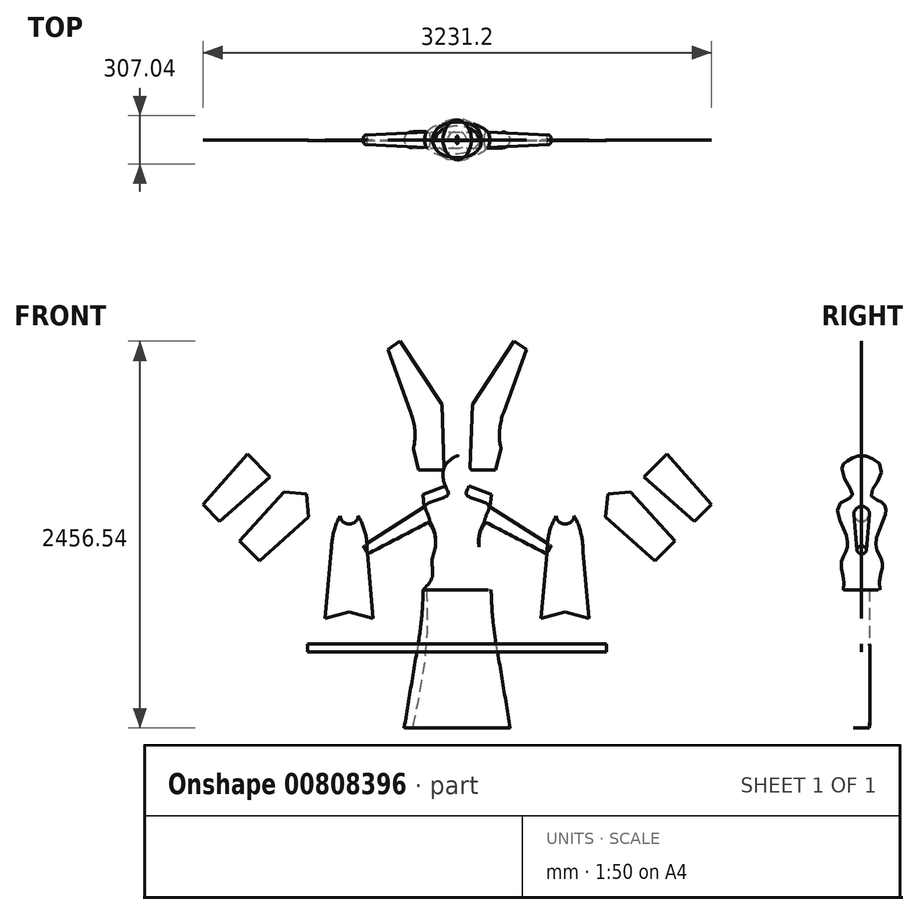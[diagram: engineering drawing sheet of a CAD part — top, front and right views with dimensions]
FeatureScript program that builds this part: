
annotation { "Feature Type Name" : "Feature", "Feature Type Description" : "" }
export const myFeature = defineFeature(function(context is Context, id is Id, definition is map)
    precondition{}
    {
        {
            var Q0;
            Q0=qCreatedBy(makeId("Front.planeOp"),FACE);
            var sketch = newSketch(context, id + "F0", { "sketchPlane" : qUnion([Q0])});
            skLineSegment(sketch, "E0", {"start": v(0, 0) * mm, "end": v(0, -1727.2) * mm, "construction": true});
            skPoint(sketch, "E1", {"position": v(0, -50.8) * mm});
            skPoint(sketch, "E2", {"position": v(0, -203.2) * mm});
            skPoint(sketch, "E3", {"position": v(0, -241.3) * mm});
            skPoint(sketch, "E4", {"position": v(0, -304.8) * mm});
            skPoint(sketch, "E5", {"position": v(0, -431.8) * mm});
            skPoint(sketch, "E6", {"position": v(0, -609.6) * mm});
            skPoint(sketch, "E7", {"position": v(0, -660.4) * mm});
            skPoint(sketch, "E8", {"position": v(0, -787.4) * mm});
            skPoint(sketch, "E9", {"position": v(0, -850.9) * mm});
            skPoint(sketch, "E10", {"position": v(0, -1193.8) * mm});
            skSolve(sketch);
        }
        {
            var Q0;
            Q0=qCreatedBy(makeId("Top.planeOp"),FACE);
            var Q1;
            Q1=sQuery(id+"F0.wireOp",VERTEX,"E1");
            cPlane(context, id + "F1", {"entities" : qUnion([Q0, Q1]), "cplaneType" : CPlaneType.PLANE_POINT, "offset" : 25.4 * mm, "width" : 152.4 * mm, "height" : 152.4 * mm});
        }
        {
            var Q0;
            Q0=sQuery(id+"F0.wireOp",VERTEX,"E2");
            var Q1;
            Q1=qCreatedBy(makeId("Top.planeOp"),FACE);
            cPlane(context, id + "F2", {"entities" : qUnion([Q0, Q1]), "cplaneType" : CPlaneType.PLANE_POINT, "offset" : 25.4 * mm, "width" : 152.4 * mm, "height" : 152.4 * mm});
        }
        {
            var Q0;
            Q0=qCreatedBy(makeId("Top.planeOp"),FACE);
            var Q1;
            Q1=sQuery(id+"F0.wireOp",VERTEX,"E3");
            cPlane(context, id + "F3", {"entities" : qUnion([Q0, Q1]), "cplaneType" : CPlaneType.PLANE_POINT, "offset" : 25.4 * mm, "width" : 152.4 * mm, "height" : 152.4 * mm});
        }
        {
            var Q0;
            Q0=sQuery(id+"F0.wireOp",VERTEX,"E4");
            var Q1;
            Q1=qCreatedBy(makeId("Top.planeOp"),FACE);
            cPlane(context, id + "F4", {"entities" : qUnion([Q0, Q1]), "cplaneType" : CPlaneType.PLANE_POINT, "offset" : 25.4 * mm, "width" : 152.4 * mm, "height" : 152.4 * mm});
        }
        {
            var Q0;
            Q0=sQuery(id+"F0.wireOp",VERTEX,"E5");
            var Q1;
            Q1=qCreatedBy(makeId("Top.planeOp"),FACE);
            cPlane(context, id + "F5", {"entities" : qUnion([Q0, Q1]), "cplaneType" : CPlaneType.PLANE_POINT, "offset" : 25.4 * mm, "width" : 152.4 * mm, "height" : 152.4 * mm});
        }
        {
            var Q0;
            Q0=sQuery(id+"F0.wireOp",VERTEX,"E6");
            var Q1;
            Q1=qCreatedBy(makeId("Top.planeOp"),FACE);
            cPlane(context, id + "F6", {"entities" : qUnion([Q0, Q1]), "cplaneType" : CPlaneType.PLANE_POINT, "offset" : 25.4 * mm, "width" : 152.4 * mm, "height" : 152.4 * mm});
        }
        {
            var Q0;
            Q0=sQuery(id+"F0.wireOp",VERTEX,"E7");
            var Q1;
            Q1=qCreatedBy(makeId("Top.planeOp"),FACE);
            cPlane(context, id + "F7", {"entities" : qUnion([Q0, Q1]), "cplaneType" : CPlaneType.PLANE_POINT, "offset" : 25.4 * mm, "width" : 152.4 * mm, "height" : 152.4 * mm});
        }
        {
            var Q0;
            Q0=qCreatedBy(makeId("Top.planeOp"),FACE);
            var Q1;
            Q1=sQuery(id+"F0.wireOp",VERTEX,"E8");
            cPlane(context, id + "F8", {"entities" : qUnion([Q0, Q1]), "cplaneType" : CPlaneType.PLANE_POINT, "offset" : 25.4 * mm, "width" : 152.4 * mm, "height" : 152.4 * mm});
        }
        {
            var Q0;
            Q0=sQuery(id+"F0.wireOp",VERTEX,"E9");
            var Q1;
            Q1=qCreatedBy(makeId("Top.planeOp"),FACE);
            cPlane(context, id + "F9", {"entities" : qUnion([Q0, Q1]), "cplaneType" : CPlaneType.PLANE_POINT, "offset" : 25.4 * mm, "width" : 152.4 * mm, "height" : 152.4 * mm});
        }
        {
            var Q0;
            Q0=sQuery(id+"F0.wireOp",VERTEX,"E10");
            var Q1;
            Q1=qCreatedBy(makeId("Top.planeOp"),FACE);
            cPlane(context, id + "F10", {"entities" : qUnion([Q0, Q1]), "cplaneType" : CPlaneType.PLANE_POINT, "offset" : 25.4 * mm, "width" : 152.4 * mm, "height" : 152.4 * mm});
        }
        {
            var Q0;
            Q0=sQuery(id+"F0.wireOp",VERTEX,"E0.end");
            var Q1;
            Q1=qCreatedBy(makeId("Top.planeOp"),FACE);
            cPlane(context, id + "F11", {"entities" : qUnion([Q0, Q1]), "cplaneType" : CPlaneType.PLANE_POINT, "offset" : 25.4 * mm, "width" : 152.4 * mm, "height" : 152.4 * mm});
        }
        {
            var Q0;
            Q0=qCreatedBy(id+"F11.planeOp",FACE);
            var sketch = newSketch(context, id + "F12", { "sketchPlane" : qUnion([Q0])});
            skLineSegment(sketch, "E11.bottom", {"start": v(-285.75, 50.8) * mm, "end": v(285.75, 50.8) * mm});
            skLineSegment(sketch, "E11.top", {"start": v(-285.75, -50.8) * mm, "end": v(285.75, -50.8) * mm});
            skLineSegment(sketch, "E11.left", {"start": v(-285.75, 50.8) * mm, "end": v(-285.75, -50.8) * mm, "construction": true});
            skLineSegment(sketch, "E11.right", {"start": v(285.75, 50.8) * mm, "end": v(285.75, -50.8) * mm, "construction": true});
            skPoint(sketch, "E11.middle", {"position": v(0, 0) * mm});
            skArc(sketch, "E12", {"start": v(-285.75, 50.8) * mm, "mid": v(-336.55, 0) * mm, "end": v(-285.75, -50.8) * mm});
            skArc(sketch, "E13", {"start": v(285.75, -50.8) * mm, "mid": v(336.55, 0) * mm, "end": v(285.75, 50.8) * mm});
            skPoint(sketch, "E14", {"position": v(-336.55, 0) * mm});
            skPoint(sketch, "E15", {"position": v(336.55, 0) * mm});
            skSolve(sketch);
        }
        {
            var Q0;
            Q0=qCreatedBy(id+"F10.planeOp",FACE);
            var sketch = newSketch(context, id + "F13", { "sketchPlane" : qUnion([Q0])});
            skLineSegment(sketch, "E16.bottom", {"start": v(-196.85, 50.8) * mm, "end": v(196.85, 50.8) * mm});
            skLineSegment(sketch, "E16.top", {"start": v(-196.85, -50.8) * mm, "end": v(196.85, -50.8) * mm});
            skLineSegment(sketch, "E16.left", {"start": v(-196.85, 50.8) * mm, "end": v(-196.85, -50.8) * mm, "construction": true});
            skLineSegment(sketch, "E16.right", {"start": v(196.85, 50.8) * mm, "end": v(196.85, -50.8) * mm, "construction": true});
            skPoint(sketch, "E16.middle", {"position": v(0, 0) * mm});
            skArc(sketch, "E17", {"start": v(-196.85, 50.8) * mm, "mid": v(-247.65, 0) * mm, "end": v(-196.85, -50.8) * mm});
            skArc(sketch, "E18", {"start": v(196.85, -50.8) * mm, "mid": v(247.65, 0) * mm, "end": v(196.85, 50.8) * mm});
            skPoint(sketch, "E19", {"position": v(247.65, 0) * mm});
            skPoint(sketch, "E20", {"position": v(-247.65, 0) * mm});
            skSolve(sketch);
        }
        {
            var Q0;
            Q0=qCreatedBy(id+"F9.planeOp",FACE);
            var sketch = newSketch(context, id + "F14", { "sketchPlane" : qUnion([Q0])});
            skEllipse(sketch, "E21", {"center": v(0, 0) * mm, "majorRadius": 215.9 * mm, "minorRadius": 114.3 * mm, "majorAxis": v(-1, 0)});
            skSolve(sketch);
        }
        {
            var Q0;
            Q0=qCreatedBy(id+"F8.planeOp",FACE);
            var sketch = newSketch(context, id + "F15", { "sketchPlane" : qUnion([Q0])});
            skEllipse(sketch, "E22", {"center": v(0, 0) * mm, "majorRadius": 165.1 * mm, "minorRadius": 114.3 * mm, "majorAxis": v(-1, 0)});
            skSolve(sketch);
        }
        {
            var Q0;
            Q0=qCreatedBy(id+"F7.planeOp",FACE);
            var sketch = newSketch(context, id + "F16", { "sketchPlane" : qUnion([Q0])});
            skEllipse(sketch, "E23", {"center": v(0, 0) * mm, "majorRadius": 158.75 * mm, "minorRadius": 127 * mm, "majorAxis": v(-1, 0)});
            skSolve(sketch);
        }
        {
            var Q0;
            Q0=qCreatedBy(id+"F6.planeOp",FACE);
            var sketch = newSketch(context, id + "F17", { "sketchPlane" : qUnion([Q0])});
            skEllipse(sketch, "E24", {"center": v(0, 0) * mm, "majorRadius": 146.05 * mm, "minorRadius": 101.6 * mm, "majorAxis": v(1, 0)});
            skSolve(sketch);
        }
        {
            var Q0;
            Q0=qCreatedBy(id+"F5.planeOp",FACE);
            var sketch = newSketch(context, id + "F18", { "sketchPlane" : qUnion([Q0])});
            skEllipse(sketch, "E25", {"center": v(0, 0) * mm, "majorRadius": 165.1 * mm, "minorRadius": 127 * mm, "majorAxis": v(1, 0)});
            skSolve(sketch);
        }
        {
            var Q0;
            Q0=qCreatedBy(id+"F4.planeOp",FACE);
            var sketch = newSketch(context, id + "F19", { "sketchPlane" : qUnion([Q0])});
            skEllipse(sketch, "E26", {"center": v(0, 0) * mm, "majorRadius": 190.5 * mm, "minorRadius": 139.7 * mm, "majorAxis": v(1, 0)});
            skSolve(sketch);
        }
        {
            var Q0;
            Q0=qCreatedBy(id+"F3.planeOp",FACE);
            var sketch = newSketch(context, id + "F20", { "sketchPlane" : qUnion([Q0])});
            skEllipse(sketch, "E27", {"center": v(0, 0) * mm, "majorRadius": 57.15 * mm, "minorRadius": 57.15 * mm, "majorAxis": v(1, 0)});
            skSolve(sketch);
        }
        {
            var Q0;
            Q0=qCreatedBy(id+"F2.planeOp",FACE);
            var sketch = newSketch(context, id + "F21", { "sketchPlane" : qUnion([Q0])});
            skEllipse(sketch, "E28", {"center": v(0, 0) * mm, "majorRadius": 69.85 * mm, "minorRadius": 76.2 * mm, "majorAxis": v(1, 0)});
            skSolve(sketch);
        }
        {
            var Q0;
            Q0=qCreatedBy(id+"F1.planeOp",FACE);
            var sketch = newSketch(context, id + "F22", { "sketchPlane" : qUnion([Q0])});
            skEllipse(sketch, "E29", {"center": v(0, 0) * mm, "majorRadius": 69.85 * mm, "minorRadius": 114.3 * mm, "majorAxis": v(1, 0)});
            skSolve(sketch);
        }
        {
            var Q0;
            Q0=qCreatedBy(makeId("Top.planeOp"),FACE);
            var sketch = newSketch(context, id + "F23", { "sketchPlane" : qUnion([Q0])});
            skEllipse(sketch, "E30", {"center": v(0, 0) * mm, "majorRadius": 6.35 * mm, "minorRadius": 25.4 * mm, "majorAxis": v(1, 0)});
            skSolve(sketch);
        }
        {
            var Q0;
            Q0=makeQuery(id+"F14.imprint","IMPRINT",FACE,{"disambiguationData":[TD([[makeQuery(id+"F14.imprint","IMPRINT",EDGE,{"derivedFrom":sQuery(id+"F14.wireOp",EDGE,"E21")}),1.0]])]});
            var Q1;
            Q1=makeQuery(id+"F15.imprint","IMPRINT",FACE,{"disambiguationData":[TD([[makeQuery(id+"F15.imprint","IMPRINT",EDGE,{"derivedFrom":sQuery(id+"F15.wireOp",EDGE,"E22")}),1.0]])]});
            var Q2;
            Q2=makeQuery(id+"F16.imprint","IMPRINT",FACE,{"disambiguationData":[TD([[makeQuery(id+"F16.imprint","IMPRINT",EDGE,{"derivedFrom":sQuery(id+"F16.wireOp",EDGE,"E23")}),1.0]])]});
            var Q3;
            Q3=makeQuery(id+"F17.imprint","IMPRINT",FACE,{"disambiguationData":[TD([[makeQuery(id+"F17.imprint","IMPRINT",EDGE,{"derivedFrom":sQuery(id+"F17.wireOp",EDGE,"E24")}),1.0]])]});
            var Q4;
            Q4=makeQuery(id+"F18.imprint","IMPRINT",FACE,{"disambiguationData":[TD([[makeQuery(id+"F18.imprint","IMPRINT",EDGE,{"derivedFrom":sQuery(id+"F18.wireOp",EDGE,"E25")}),1.0]])]});
            var Q5;
            Q5=makeQuery(id+"F19.imprint","IMPRINT",FACE,{"disambiguationData":[TD([[makeQuery(id+"F19.imprint","IMPRINT",EDGE,{"derivedFrom":sQuery(id+"F19.wireOp",EDGE,"E26")}),1.0]])]});
            var Q6;
            Q6=makeQuery(id+"F20.imprint","IMPRINT",FACE,{"disambiguationData":[TD([[makeQuery(id+"F20.imprint","IMPRINT",EDGE,{"derivedFrom":sQuery(id+"F20.wireOp",EDGE,"E27")}),1.0]])]});
            var Q7;
            Q7=makeQuery(id+"F21.imprint","IMPRINT",FACE,{"disambiguationData":[TD([[makeQuery(id+"F21.imprint","IMPRINT",EDGE,{"derivedFrom":sQuery(id+"F21.wireOp",EDGE,"E28")}),1.0]])]});
            var Q8;
            Q8=makeQuery(id+"F22.imprint","IMPRINT",FACE,{"disambiguationData":[TD([[makeQuery(id+"F22.imprint","IMPRINT",EDGE,{"derivedFrom":sQuery(id+"F22.wireOp",EDGE,"E29")}),1.0]])]});
            var Q9;
            Q9=makeQuery(id+"F23.imprint","IMPRINT",FACE,{"disambiguationData":[TD([[makeQuery(id+"F23.imprint","IMPRINT",EDGE,{"derivedFrom":sQuery(id+"F23.wireOp",EDGE,"E30")}),1.0]])]});
            loft(context, id + "F24", {"sheetProfilesArray" : [{ "sheetProfileEntities" : qUnion([Q0]) }, { "sheetProfileEntities" : qUnion([Q1]) }, { "sheetProfileEntities" : qUnion([Q2]) }, { "sheetProfileEntities" : qUnion([Q3]) }, { "sheetProfileEntities" : qUnion([Q4]) }, { "sheetProfileEntities" : qUnion([Q5]) }, { "sheetProfileEntities" : qUnion([Q6]) }, { "sheetProfileEntities" : qUnion([Q7]) }, { "sheetProfileEntities" : qUnion([Q8]) }, { "sheetProfileEntities" : qUnion([Q9]) }]});
        }
        {
            var Q1;
            Q1=makeQuery(id+"F24.opLoft","CAP_FACE",FACE,{"disambiguationData":[OSD([makeQuery(id+"F14.imprint","IMPRINT",FACE,{"disambiguationData":[TD([[makeQuery(id+"F14.imprint","IMPRINT",EDGE,{"derivedFrom":sQuery(id+"F14.wireOp",EDGE,"E21")}),1.0]])]})])],"isStart":true});
            var Q2;
            Q2=makeQuery(id+"F13.imprint","IMPRINT",FACE,{"disambiguationData":[TD([[makeQuery(id+"F13.imprint","IMPRINT",EDGE,{"derivedFrom":sQuery(id+"F13.wireOp",EDGE,"E16.bottom")}),-1.0]])]});
            var Q3;
            Q3=makeQuery(id+"F12.imprint","IMPRINT",FACE,{"disambiguationData":[TD([[makeQuery(id+"F12.imprint","IMPRINT",EDGE,{"derivedFrom":sQuery(id+"F12.wireOp",EDGE,"E11.bottom")}),-1.0]])]});
            loft(context, id + "F25", {"operationType" : NewBodyOperationType.ADD, "sheetProfilesArray" : [{ "sheetProfileEntities" : qUnion([Q1]) }, { "sheetProfileEntities" : qUnion([Q2]) }, { "sheetProfileEntities" : qUnion([Q3]) }]});
        }
        {
            var Q0;
            Q0=qCreatedBy(makeId("Front.planeOp"),FACE);
            var sketch = newSketch(context, id + "F26", { "sketchPlane" : qUnion([Q0])});
            skPoint(sketch, "E31.0", {"position": v(0, -304.8) * mm});
            skLineSegment(sketch, "E32", {"start": v(0, -304.8) * mm, "end": v(-165.1, -355.6) * mm});
            skLineSegment(sketch, "E33", {"start": v(-165.1, -355.6) * mm, "end": v(-583.04, -596.9) * mm});
            skLineSegment(sketch, "E34", {"start": v(-608.44, -552.9) * mm, "end": v(-583.04, -596.9) * mm});
            skLineSegment(sketch, "E35", {"start": v(-165.1, -355.6) * mm, "end": v(-190.5, -311.6) * mm});
            skSolve(sketch);
        }
        {
            var Q0;
            Q0=sQuery(id+"F26.wireOp",EDGE,"E34");
            cPlane(context, id + "F27", {"entities" : qUnion([Q0]), "cplaneType" : CPlaneType.LINE_ANGLE, "offset" : 25.4 * mm, "angle" : 180 * degree, "width" : 152.4 * mm, "height" : 152.4 * mm});
        }
        {
            var Q0;
            Q0=sQuery(id+"F26.wireOp",EDGE,"E35");
            cPlane(context, id + "F28", {"entities" : qUnion([Q0]), "cplaneType" : CPlaneType.LINE_ANGLE, "offset" : 25.4 * mm, "angle" : 180 * degree, "width" : 152.4 * mm, "height" : 152.4 * mm});
        }
        {
            var Q0;
            Q0=qCreatedBy(id+"F28.planeOp",FACE);
            var sketch = newSketch(context, id + "F29", { "sketchPlane" : qUnion([Q0])});
            skPoint(sketch, "E36.0", {"position": v(0, -225.4) * mm});
            skCircle(sketch, "E37", {"center": v(0, -225.4) * mm, "radius": 50.8 * mm});
            skSolve(sketch);
        }
        {
            var Q0;
            Q0=qCreatedBy(id+"F27.planeOp",FACE);
            var sketch = newSketch(context, id + "F30", { "sketchPlane" : qUnion([Q0])});
            skPoint(sketch, "E38.0", {"position": v(0, -225.4) * mm});
            skCircle(sketch, "E39", {"center": v(0, -225.4) * mm, "radius": 29.21 * mm});
            skSolve(sketch);
        }
        {
            var Q0;
            Q0=makeQuery(id+"F29.imprint","IMPRINT",FACE,{"disambiguationData":[TD([[makeQuery(id+"F29.imprint","IMPRINT",EDGE,{"derivedFrom":sQuery(id+"F29.wireOp",EDGE,"E37")}),1.0]])]});
            var Q1;
            Q1=makeQuery(id+"F30.imprint","IMPRINT",FACE,{"disambiguationData":[TD([[makeQuery(id+"F30.imprint","IMPRINT",EDGE,{"derivedFrom":sQuery(id+"F30.wireOp",EDGE,"E39")}),1.0]])]});
            loft(context, id + "F31", {"sheetProfilesArray" : [{ "sheetProfileEntities" : qUnion([Q0]) }, { "sheetProfileEntities" : qUnion([Q1]) }]});
        }
        {
            var Q0;
            Q0=makeQuery(id+"F31.opLoft","SWEPT_BODY",BODY,{"disambiguationData":[OSD([makeQuery(id+"F29.imprint","IMPRINT",FACE,{"disambiguationData":[TD([[makeQuery(id+"F29.imprint","IMPRINT",EDGE,{"derivedFrom":sQuery(id+"F29.wireOp",EDGE,"E37")}),1.0]])]}),makeQuery(id+"F30.imprint","IMPRINT",FACE,{"disambiguationData":[TD([[makeQuery(id+"F30.imprint","IMPRINT",EDGE,{"derivedFrom":sQuery(id+"F30.wireOp",EDGE,"E39")}),1.0]])]})])]});
            var Q1;
            Q1=qCreatedBy(makeId("Right.planeOp"),FACE);
            mirror(context, id + "F32", {"entities" : qUnion([Q0]), "mirrorPlane" : qUnion([Q1])});
        }
        {
            var Q0;
            Q0=qCreatedBy(makeId("Front.planeOp"),FACE);
            var sketch = newSketch(context, id + "F33", { "sketchPlane" : qUnion([Q0])});
            skLineSegment(sketch, "E40", {"start": v(0, -1066.8) * mm, "end": v(0, -177.8) * mm, "construction": true});
            skLineSegment(sketch, "E41", {"start": v(0, -1066.8) * mm, "end": v(-127, -1032.77) * mm});
            skLineSegment(sketch, "E42", {"start": v(0, -609.6) * mm, "end": v(-127, -609.6) * mm, "construction": true});
            skLineSegment(sketch, "E43", {"start": v(-127, -1032.77) * mm, "end": v(-127, -609.6) * mm});
            skLineSegment(sketch, "E44", {"start": v(-190.5, -381) * mm, "end": v(-127, -609.6) * mm, "construction": true});
            skLineSegment(sketch, "E45", {"start": v(-127, -1032.77) * mm, "end": v(0, -1032.77) * mm, "construction": true});
            skLineSegment(sketch, "E46", {"start": v(-190.5, -381) * mm, "end": v(0, -381) * mm, "construction": true});
            skFitSpline(sketch, "E47", {"points": [v(-127, -609.6) * mm, v(-132.13, -487.9) * mm, v(-190.5, -381) * mm], "startDerivative": vector(0, 266.7) * mm, "endDerivative": vector(-127.8, 234.08) * mm});
            skLineSegment(sketch, "E48", {"start": v(-127, -609.6) * mm, "end": v(-132.13, -487.9) * mm, "construction": true});
            skLineSegment(sketch, "E49", {"start": v(-190.5, -381) * mm, "end": v(-132.13, -487.9) * mm, "construction": true});
            skLineSegment(sketch, "E50", {"start": v(-132.13, -487.9) * mm, "end": v(0, -469.9) * mm, "construction": true});
            skLineSegment(sketch, "E51", {"start": v(-169.2, -420.01) * mm, "end": v(-190.5, -381) * mm, "construction": true});
            skLineSegment(sketch, "E52", {"start": v(-190.5, -381) * mm, "end": v(-203.2, -254) * mm});
            skLineSegment(sketch, "E53", {"start": v(-60.96, -200.66) * mm, "end": v(-203.2, -254) * mm});
            skLineSegment(sketch, "E54.MirrorCS", {"start": v(0, -1066.8) * mm, "end": v(127, -1032.77) * mm});
            skLineSegment(sketch, "E55.MirrorCS", {"start": v(127, -1032.77) * mm, "end": v(127, -609.6) * mm});
            skFitSpline(sketch, "E56.MirrorCS", {"points": [v(127, -609.6) * mm, v(132.13, -487.9) * mm, v(190.5, -381) * mm], "startDerivative": vector(0, 266.7) * mm, "endDerivative": vector(127.8, 234.08) * mm});
            skLineSegment(sketch, "E57.MirrorCS", {"start": v(190.5, -381) * mm, "end": v(203.2, -254) * mm});
            skLineSegment(sketch, "E58.MirrorCS", {"start": v(60.96, -200.66) * mm, "end": v(203.2, -254) * mm});
            skPoint(sketch, "E59.orphan", {"position": v(0, -177.8) * mm});
            skEllipticalArc(sketch, "E60", {});
            skLineSegment(sketch, "E61", {"start": v(-969, -254) * mm, "end": v(-1319.23, -604.23) * mm, "construction": true});
            skLineSegment(sketch, "E62", {"start": v(-969, -254) * mm, "end": v(-956.3, -381) * mm});
            skLineSegment(sketch, "E63", {"start": v(-956.3, -381) * mm, "end": v(-1265.35, -658.11) * mm});
            skLineSegment(sketch, "E64", {"start": v(-969, -254) * mm, "end": v(-969, -392.39) * mm, "construction": true});
            skLineSegment(sketch, "E65.MirrorCS", {"start": v(-969, -254) * mm, "end": v(-1096, -241.3) * mm});
            skLineSegment(sketch, "E66.MirrorCS", {"start": v(-1096, -241.3) * mm, "end": v(-1373.11, -550.35) * mm});
            skLineSegment(sketch, "E67", {"start": v(-1265.35, -658.11) * mm, "end": v(-1319.23, -604.23) * mm});
            skLineSegment(sketch, "E68", {"start": v(-1373.11, -550.35) * mm, "end": v(-1319.23, -604.23) * mm});
            skLineSegment(sketch, "E69", {"start": v(0, -126.22) * mm, "end": v(-149.6, -152.6) * mm, "construction": true});
            skLineSegment(sketch, "E70.MirrorCS", {"start": v(-82.74, -77.11) * mm, "end": v(-234.65, -75.64) * mm});
            skLineSegment(sketch, "E71.MirrorCS", {"start": v(-266.15, 48.05) * mm, "end": v(-234.65, -75.64) * mm});
            skLineSegment(sketch, "E72.MirrorCS", {"start": v(-165.33, 328.02) * mm, "end": v(-284.67, 284.58) * mm, "construction": true});
            skLineSegment(sketch, "E73.MirrorCS", {"start": v(-429.4, 682.23) * mm, "end": v(-310.06, 725.67) * mm, "construction": true});
            skLineSegment(sketch, "E74.MirrorCS", {"start": v(-321.7, 757.64) * mm, "end": v(-17.64, -77.74) * mm, "construction": true});
            skLineSegment(sketch, "E75", {"start": v(-82.74, -77.11) * mm, "end": v(-97.75, 328.02) * mm});
            skLineSegment(sketch, "E76", {"start": v(-97.75, 328.02) * mm, "end": v(-362.12, 729.34) * mm});
            skFitSpline(sketch, "E77", {"points": [v(-266.15, 48.05) * mm, v(-284.67, 284.58) * mm], "startDerivative": vector(61.9, 220.06) * mm, "endDerivative": vector(-78.19, 214.81) * mm});
            skLineSegment(sketch, "E78", {"start": v(-284.67, 284.58) * mm, "end": v(-429.4, 682.23) * mm});
            skLineSegment(sketch, "E79", {"start": v(-429.4, 682.23) * mm, "end": v(-362.12, 729.34) * mm});
            skPoint(sketch, "E80", {"position": v(-248.76, 557.26) * mm});
            skLineSegment(sketch, "E81", {"start": v(-284.67, 284.58) * mm, "end": v(-547.22, 189.02) * mm, "construction": true});
            skLineSegment(sketch, "E82.MirrorCS", {"start": v(0, -609.6) * mm, "end": v(127, -609.6) * mm, "construction": true});
            skLineSegment(sketch, "E83", {"start": v(-245.52, 121.4) * mm, "end": v(-266.15, 48.05) * mm, "construction": true});
            skLineSegment(sketch, "E84", {"start": v(-258.6, 212.97) * mm, "end": v(-284.67, 284.58) * mm, "construction": true});
            skLineSegment(sketch, "E85.MirrorCS", {"start": v(82.74, -77.11) * mm, "end": v(97.75, 328.02) * mm});
            skLineSegment(sketch, "E86.MirrorCS", {"start": v(82.74, -77.11) * mm, "end": v(234.65, -75.64) * mm});
            skLineSegment(sketch, "E87.MirrorCS", {"start": v(266.15, 48.05) * mm, "end": v(234.65, -75.64) * mm});
            skFitSpline(sketch, "E88.MirrorCS", {"points": [v(266.15, 48.05) * mm, v(284.67, 284.58) * mm], "startDerivative": vector(-61.9, 220.06) * mm, "endDerivative": vector(78.19, 214.81) * mm});
            skLineSegment(sketch, "E89.MirrorCS", {"start": v(284.67, 284.58) * mm, "end": v(429.4, 682.23) * mm});
            skLineSegment(sketch, "E90.MirrorCS", {"start": v(97.75, 328.02) * mm, "end": v(362.12, 729.34) * mm});
            skLineSegment(sketch, "E91.MirrorCS", {"start": v(429.4, 682.23) * mm, "end": v(362.12, 729.34) * mm});
            skLineSegment(sketch, "E92", {"start": v(-321.7, 757.64) * mm, "end": v(-441.04, 714.2) * mm, "construction": true});
            skLineSegment(sketch, "E93", {"start": v(-266.15, 48.05) * mm, "end": v(-284.67, 284.58) * mm, "construction": true});
            skLineSegment(sketch, "E94", {"start": v(-266.15, 48.05) * mm, "end": v(-344.34, 262.86) * mm, "construction": true});
            skLineSegment(sketch, "E95.MirrorCS", {"start": v(-127, -1032.77) * mm, "end": v(-47.67, -1054.03) * mm, "construction": true});
            skLineSegment(sketch, "E96.MirrorCS", {"start": v(-321.7, 757.64) * mm, "end": v(-429.4, 682.23) * mm});
            skPoint(sketch, "E97", {"position": v(-628.65, -381) * mm});
            skPoint(sketch, "E98", {"position": v(-742.95, -381) * mm});
            skLineSegment(sketch, "E99", {"start": v(-571.5, -609.6) * mm, "end": v(-533.4, -1032.77) * mm});
            skLineSegment(sketch, "E100", {"start": v(-628.65, -381) * mm, "end": v(-742.95, -381) * mm, "construction": true});
            skLineSegment(sketch, "E101", {"start": v(-685.8, -381) * mm, "end": v(-685.8, -1066.8) * mm, "construction": true});
            skEllipticalArc(sketch, "E102", {});
            skLineSegment(sketch, "E103", {"start": v(-571.5, -609.6) * mm, "end": v(-685.8, -609.6) * mm, "construction": true});
            skLineSegment(sketch, "E104.MirrorCS", {"start": v(-800.1, -609.6) * mm, "end": v(-685.8, -609.6) * mm, "construction": true});
            skLineSegment(sketch, "E105", {"start": v(-533.4, -1032.77) * mm, "end": v(-685.8, -991.93) * mm});
            skLineSegment(sketch, "E106", {"start": v(-685.8, -991.93) * mm, "end": v(-838.2, -1032.77) * mm});
            skLineSegment(sketch, "E107", {"start": v(-838.2, -1032.77) * mm, "end": v(-800.1, -609.6) * mm});
            skFitSpline(sketch, "E108", {"points": [v(-800.1, -609.6) * mm, v(-742.95, -381) * mm], "startDerivative": vector(0, 228.6) * mm, "endDerivative": vector(114.3, 197.97) * mm});
            skFitSpline(sketch, "E109", {"points": [v(-571.5, -609.6) * mm, v(-584.2, -487.9) * mm, v(-628.65, -381) * mm], "startDerivative": vector(0, 263.07) * mm, "endDerivative": vector(-129.6, 237.36) * mm});
            skLineSegment(sketch, "E110", {"start": v(-800.1, -609.6) * mm, "end": v(-800.1, -533.4) * mm, "construction": true});
            skLineSegment(sketch, "E111", {"start": v(-781.05, -447) * mm, "end": v(-742.95, -381) * mm, "construction": true});
            skLineSegment(sketch, "E112", {"start": v(-607.35, -420.01) * mm, "end": v(-628.65, -381) * mm, "construction": true});
            skLineSegment(sketch, "E113", {"start": v(-571.5, -609.6) * mm, "end": v(-571.5, -565.15) * mm, "construction": true});
            skFitSpline(sketch, "E114.MirrorCS", {"points": [v(571.5, -609.6) * mm, v(584.2, -487.9) * mm, v(628.65, -381) * mm], "startDerivative": vector(0, 263.07) * mm, "endDerivative": vector(129.6, 237.36) * mm});
            skLineSegment(sketch, "E115.MirrorCS", {"start": v(571.5, -609.6) * mm, "end": v(533.4, -1032.77) * mm});
            skEllipticalArc(sketch, "E116.MirrorCS", {});
            skFitSpline(sketch, "E117.MirrorCS", {"points": [v(800.1, -609.6) * mm, v(742.95, -381) * mm], "startDerivative": vector(0, 228.6) * mm, "endDerivative": vector(-114.3, 197.97) * mm});
            skLineSegment(sketch, "E118.MirrorCS", {"start": v(838.2, -1032.77) * mm, "end": v(800.1, -609.6) * mm});
            skLineSegment(sketch, "E119.MirrorCS", {"start": v(685.8, -991.93) * mm, "end": v(838.2, -1032.77) * mm});
            skLineSegment(sketch, "E120.MirrorCS", {"start": v(533.4, -1032.77) * mm, "end": v(685.8, -991.93) * mm});
            skLineSegment(sketch, "E121", {"start": v(-956.3, -381) * mm, "end": v(-1096, -241.3) * mm, "construction": true});
            skLineSegment(sketch, "E122", {"start": v(-1561.7, -361.76) * mm, "end": v(-1268.73, -68.8) * mm, "construction": true});
            skLineSegment(sketch, "E123", {"start": v(-1561.7, -361.76) * mm, "end": v(-1516.8, -406.66) * mm});
            skLineSegment(sketch, "E124", {"start": v(-1516.8, -406.66) * mm, "end": v(-1205.87, -131.66) * mm});
            skLineSegment(sketch, "E125", {"start": v(-1268.73, -68.8) * mm, "end": v(-1205.87, -131.66) * mm, "construction": true});
            skLineSegment(sketch, "E126", {"start": v(-1373.11, -550.35) * mm, "end": v(-1516.8, -406.66) * mm, "construction": true});
            skLineSegment(sketch, "E127.MirrorCS", {"start": v(-1561.7, -361.76) * mm, "end": v(-1606.6, -316.86) * mm});
            skLineSegment(sketch, "E128.MirrorCS", {"start": v(-1606.6, -316.86) * mm, "end": v(-1331.6, -5.94) * mm});
            skLineSegment(sketch, "E129", {"start": v(-685.8, -431.8) * mm, "end": v(-190.5, -431.8) * mm, "construction": true});
            skLineSegment(sketch, "E130", {"start": v(-190.5, -431.8) * mm, "end": v(-159.55, -431.8) * mm, "construction": true});
            skLineSegment(sketch, "E131", {"start": v(-1205.87, -131.66) * mm, "end": v(-1331.6, -5.94) * mm});
            skLineSegment(sketch, "E132", {"start": v(-203.2, -254) * mm, "end": v(-553.43, -604.23) * mm, "construction": true});
            skLineSegment(sketch, "E133", {"start": v(-190.5, -381) * mm, "end": v(-499.55, -658.11) * mm, "construction": true});
            skLineSegment(sketch, "E134", {"start": v(-159.55, -431.8) * mm, "end": v(-490.04, -681.67) * mm, "construction": true});
            skLineSegment(sketch, "E135", {"start": v(-490.04, -681.67) * mm, "end": v(-499.55, -658.11) * mm, "construction": true});
            skLineSegment(sketch, "E136", {"start": v(-553.43, -604.23) * mm, "end": v(-499.55, -658.11) * mm, "construction": true});
            skLineSegment(sketch, "E137.MirrorCS", {"start": v(956.3, -381) * mm, "end": v(1265.35, -658.11) * mm});
            skLineSegment(sketch, "E138.MirrorCS", {"start": v(969, -254) * mm, "end": v(956.3, -381) * mm});
            skLineSegment(sketch, "E139.MirrorCS", {"start": v(969, -254) * mm, "end": v(1096, -241.3) * mm});
            skLineSegment(sketch, "E140.MirrorCS", {"start": v(1096, -241.3) * mm, "end": v(1373.11, -550.35) * mm});
            skLineSegment(sketch, "E141.MirrorCS", {"start": v(1373.11, -550.35) * mm, "end": v(1319.23, -604.23) * mm});
            skLineSegment(sketch, "E142.MirrorCS", {"start": v(1265.35, -658.11) * mm, "end": v(1319.23, -604.23) * mm});
            skLineSegment(sketch, "E143.MirrorCS", {"start": v(1561.7, -361.76) * mm, "end": v(1516.8, -406.66) * mm});
            skLineSegment(sketch, "E144.MirrorCS", {"start": v(1561.7, -361.76) * mm, "end": v(1606.6, -316.86) * mm});
            skLineSegment(sketch, "E145.MirrorCS", {"start": v(1606.6, -316.86) * mm, "end": v(1331.6, -5.94) * mm});
            skLineSegment(sketch, "E146.MirrorCS", {"start": v(1516.8, -406.66) * mm, "end": v(1205.87, -131.66) * mm});
            skLineSegment(sketch, "E147.MirrorCS", {"start": v(1205.87, -131.66) * mm, "end": v(1331.6, -5.94) * mm});
            skLineSegment(sketch, "E148", {"start": v(-1469.1, -161.4) * mm, "end": v(-1361.33, -269.16) * mm, "construction": true});
            skLineSegment(sketch, "E149", {"start": v(-1234.56, -395.82) * mm, "end": v(-1103.7, -513.16) * mm, "construction": true});
            skLineSegment(sketch, "E150.bottom", {"start": v(-949.48, -1193.8) * mm, "end": v(949.48, -1193.8) * mm});
            skLineSegment(sketch, "E150.top", {"start": v(-949.48, -1244.6) * mm, "end": v(949.48, -1244.6) * mm});
            skLineSegment(sketch, "E150.left", {"start": v(-949.48, -1193.8) * mm, "end": v(-949.48, -1244.6) * mm});
            skLineSegment(sketch, "E150.right", {"start": v(949.48, -1193.8) * mm, "end": v(949.48, -1244.6) * mm});
            skPoint(sketch, "E150.middle", {"position": v(0, -1219.2) * mm});
            skLineSegment(sketch, "E151", {"start": v(-63.5, -1219.2) * mm, "end": v(0, -1219.2) * mm, "construction": true});
            skLineSegment(sketch, "E152", {"start": v(-63.5, -1219.2) * mm, "end": v(-468.9, -1219.2) * mm, "construction": true});
            skLineSegment(sketch, "E153", {"start": v(-468.9, -1219.2) * mm, "end": v(-949.48, -1219.2) * mm, "construction": true});
            skLineSegment(sketch, "E154.MirrorCS", {"start": v(63.5, -1219.2) * mm, "end": v(0, -1219.2) * mm, "construction": true});
            skLineSegment(sketch, "E155.MirrorCS", {"start": v(63.5, -1219.2) * mm, "end": v(468.9, -1219.2) * mm, "construction": true});
            skLineSegment(sketch, "E156.MirrorCS", {"start": v(468.9, -1219.2) * mm, "end": v(949.48, -1219.2) * mm, "construction": true});
            const initialGuessF33  = {"E60": [0, -0.1778, 1, 0, 0.0762, 0.0381, 3.7850937623830347, 5.6396841983863455], "E102": [-0.6858, -0.381, -1, 0, 0.05715, 0.0508, 0, 3.141592653589793], "E116.MirrorCS": [0.6858, -0.381, 1, 0, 0.05715, 0.0508, 3.141592653589793, 0]};
            skSetInitialGuess(sketch, initialGuessF33);
            skSolve(sketch);
        }
        {
            var Q0;
            Q0=makeQuery(id+"F33.imprint","IMPRINT",FACE,{"disambiguationData":[TD([[makeQuery(id+"F33.imprint","IMPRINT",EDGE,{"derivedFrom":sQuery(id+"F33.wireOp",EDGE,"E41")}),-1.0]])]});
            var Q1;
            Q1=makeQuery(id+"F33.imprint","IMPRINT",FACE,{"disambiguationData":[TD([[makeQuery(id+"F33.imprint","IMPRINT",EDGE,{"derivedFrom":sQuery(id+"F33.wireOp",EDGE,"E85.MirrorCS")}),-1.0]])]});
            var Q2;
            Q2=makeQuery(id+"F33.imprint","IMPRINT",FACE,{"disambiguationData":[TD([[makeQuery(id+"F33.imprint","IMPRINT",EDGE,{"derivedFrom":sQuery(id+"F33.wireOp",EDGE,"E70.MirrorCS")}),-1.0]])]});
            var Q3;
            Q3=makeQuery(id+"F33.imprint","IMPRINT",FACE,{"disambiguationData":[TD([[makeQuery(id+"F33.imprint","IMPRINT",EDGE,{"derivedFrom":sQuery(id+"F33.wireOp",EDGE,"E99")}),-1.0]])]});
            var Q4;
            Q4=makeQuery(id+"F33.imprint","IMPRINT",FACE,{"disambiguationData":[TD([[makeQuery(id+"F33.imprint","IMPRINT",EDGE,{"derivedFrom":sQuery(id+"F33.wireOp",EDGE,"E62")}),-1.0]])]});
            var Q5;
            Q5=makeQuery(id+"F33.imprint","IMPRINT",FACE,{"disambiguationData":[TD([[makeQuery(id+"F33.imprint","IMPRINT",EDGE,{"derivedFrom":sQuery(id+"F33.wireOp",EDGE,"E123")}),1.0]])]});
            var Q6;
            Q6=makeQuery(id+"F33.imprint","IMPRINT",FACE,{"disambiguationData":[TD([[makeQuery(id+"F33.imprint","IMPRINT",EDGE,{"derivedFrom":sQuery(id+"F33.wireOp",EDGE,"E114.MirrorCS")}),-1.0]])]});
            var Q7;
            Q7=makeQuery(id+"F33.imprint","IMPRINT",FACE,{"disambiguationData":[TD([[makeQuery(id+"F33.imprint","IMPRINT",EDGE,{"derivedFrom":sQuery(id+"F33.wireOp",EDGE,"E137.MirrorCS")}),1.0]])]});
            var Q8;
            Q8=makeQuery(id+"F33.imprint","IMPRINT",FACE,{"disambiguationData":[TD([[makeQuery(id+"F33.imprint","IMPRINT",EDGE,{"derivedFrom":sQuery(id+"F33.wireOp",EDGE,"E143.MirrorCS")}),-1.0]])]});
            extrude(context, id + "F34", {"entities" : qUnion([Q0, Q1, Q2, Q3, Q4, Q5, Q6, Q7, Q8]), "depth" : 1.59 * mm, "offsetDistance" : 25.4 * mm});
        }
        {
            var Q0;
            Q0=makeQuery(id+"F34.opExtrude","CAP_FACE",FACE,{"disambiguationData":[OSD([sQuery(id+"F33.wireOp",EDGE,"E41"),sQuery(id+"F33.wireOp",EDGE,"E43"),sQuery(id+"F33.wireOp",EDGE,"E47"),sQuery(id+"F33.wireOp",EDGE,"E52"),sQuery(id+"F33.wireOp",EDGE,"E53"),sQuery(id+"F33.wireOp",EDGE,"E54.MirrorCS"),sQuery(id+"F33.wireOp",EDGE,"E55.MirrorCS"),sQuery(id+"F33.wireOp",EDGE,"E56.MirrorCS"),sQuery(id+"F33.wireOp",EDGE,"E57.MirrorCS"),sQuery(id+"F33.wireOp",EDGE,"E58.MirrorCS"),sQuery(id+"F33.wireOp",EDGE,"E60")])],"isStart":false});
            var sketch = newSketch(context, id + "F35", { "sketchPlane" : qUnion([Q0])});
            skLineSegment(sketch, "E157.0", {"start": v(-127, -1032.77) * mm, "end": v(-127, -609.6) * mm});
            skFitSpline(sketch, "E157.1", {"points": [v(-127, -609.6) * mm, v(-127, -565.15) * mm, v(-116.16, -483.23) * mm, v(-169.2, -420.01) * mm, v(-190.5, -381) * mm]});
            skLineSegment(sketch, "E157.2", {"start": v(-190.5, -381) * mm, "end": v(-203.2, -254) * mm});
            skLineSegment(sketch, "E157.3", {"start": v(-60.96, -200.66) * mm, "end": v(-203.2, -254) * mm});
            skLineSegment(sketch, "E157.4", {"start": v(60.96, -200.66) * mm, "end": v(203.2, -254) * mm});
            skLineSegment(sketch, "E157.5", {"start": v(190.5, -381) * mm, "end": v(203.2, -254) * mm});
            skFitSpline(sketch, "E157.6", {"points": [v(127, -609.6) * mm, v(127, -565.15) * mm, v(116.16, -483.23) * mm, v(169.2, -420.01) * mm, v(190.5, -381) * mm]});
            skLineSegment(sketch, "E157.7", {"start": v(127, -1032.77) * mm, "end": v(127, -609.6) * mm});
            skLineSegment(sketch, "E158.0", {"start": v(-838.2, -1032.77) * mm, "end": v(-800.1, -609.6) * mm});
            skLineSegment(sketch, "E158.1", {"start": v(-571.5, -609.6) * mm, "end": v(-533.4, -1032.77) * mm});
            skFitSpline(sketch, "E158.2", {"points": [v(-571.5, -609.6) * mm, v(-571.5, -565.15) * mm, v(-578.48, -485.23) * mm, v(-607.35, -420.01) * mm, v(-628.65, -381) * mm]});
            skFitSpline(sketch, "E158.3", {"points": [v(-800.1, -609.6) * mm, v(-800.1, -533.4) * mm, v(-781.05, -447) * mm, v(-742.95, -381) * mm]});
            skLineSegment(sketch, "E159.0", {"start": v(-956.3, -381) * mm, "end": v(-1265.35, -658.11) * mm});
            skLineSegment(sketch, "E159.1", {"start": v(-969, -254) * mm, "end": v(-956.3, -381) * mm});
            skLineSegment(sketch, "E159.2", {"start": v(-969, -254) * mm, "end": v(-1096, -241.3) * mm});
            skLineSegment(sketch, "E159.3", {"start": v(-1096, -241.3) * mm, "end": v(-1373.11, -550.35) * mm});
            skLineSegment(sketch, "E159.4", {"start": v(-1516.8, -406.66) * mm, "end": v(-1205.87, -131.66) * mm});
            skLineSegment(sketch, "E159.5", {"start": v(-1205.87, -131.66) * mm, "end": v(-1331.6, -5.94) * mm});
            skLineSegment(sketch, "E159.6", {"start": v(-1606.6, -316.86) * mm, "end": v(-1331.6, -5.94) * mm});
            skFitSpline(sketch, "E160.0", {"points": [v(571.5, -609.6) * mm, v(571.5, -565.15) * mm, v(578.48, -485.23) * mm, v(607.35, -420.01) * mm, v(628.65, -381) * mm]});
            skLineSegment(sketch, "E160.1", {"start": v(571.5, -609.6) * mm, "end": v(533.4, -1032.77) * mm});
            skLineSegment(sketch, "E160.2", {"start": v(838.2, -1032.77) * mm, "end": v(800.1, -609.6) * mm});
            skFitSpline(sketch, "E160.3", {"points": [v(800.1, -609.6) * mm, v(800.1, -533.4) * mm, v(781.05, -447) * mm, v(742.95, -381) * mm]});
            skLineSegment(sketch, "E161.0", {"start": v(956.3, -381) * mm, "end": v(1265.35, -658.11) * mm});
            skLineSegment(sketch, "E161.1", {"start": v(969, -254) * mm, "end": v(956.3, -381) * mm});
            skLineSegment(sketch, "E161.2", {"start": v(969, -254) * mm, "end": v(1096, -241.3) * mm});
            skLineSegment(sketch, "E161.3", {"start": v(1096, -241.3) * mm, "end": v(1373.11, -550.35) * mm});
            skLineSegment(sketch, "E161.4", {"start": v(1516.8, -406.66) * mm, "end": v(1205.87, -131.66) * mm});
            skLineSegment(sketch, "E161.5", {"start": v(1205.87, -131.66) * mm, "end": v(1331.6, -5.94) * mm});
            skLineSegment(sketch, "E161.6", {"start": v(1606.6, -316.86) * mm, "end": v(1331.6, -5.94) * mm});
            skLineSegment(sketch, "E162.0", {"start": v(-82.74, -77.11) * mm, "end": v(-234.65, -75.64) * mm});
            skLineSegment(sketch, "E162.1", {"start": v(-266.15, 48.05) * mm, "end": v(-234.65, -75.64) * mm});
            skFitSpline(sketch, "E162.2", {"points": [v(-266.15, 48.05) * mm, v(-245.52, 121.4) * mm, v(-258.6, 212.97) * mm, v(-284.67, 284.58) * mm]});
            skLineSegment(sketch, "E162.3", {"start": v(-284.67, 284.58) * mm, "end": v(-429.4, 682.23) * mm});
            skLineSegment(sketch, "E162.4", {"start": v(82.74, -77.11) * mm, "end": v(234.65, -75.64) * mm});
            skLineSegment(sketch, "E162.5", {"start": v(266.15, 48.05) * mm, "end": v(234.65, -75.64) * mm});
            skFitSpline(sketch, "E162.6", {"points": [v(266.15, 48.05) * mm, v(245.52, 121.4) * mm, v(258.6, 212.97) * mm, v(284.67, 284.58) * mm]});
            skLineSegment(sketch, "E162.7", {"start": v(284.67, 284.58) * mm, "end": v(429.4, 682.23) * mm});
            skLineSegment(sketch, "E163.0", {"start": v(-60.96, -187.1) * mm, "end": v(-216.8, -245.54) * mm});
            skLineSegment(sketch, "E163.1", {"start": v(-202.88, -384.85) * mm, "end": v(-216.8, -245.54) * mm});
            skLineSegment(sketch, "E164", {"start": v(-60.96, -200.66) * mm, "end": v(-60.96, -187.1) * mm});
            skLineSegment(sketch, "E165.0", {"start": v(-139.7, -1032.77) * mm, "end": v(-139.7, -609.6) * mm});
            skLineSegment(sketch, "E166", {"start": v(-139.7, -1032.77) * mm, "end": v(-127, -1032.77) * mm});
            skFitSpline(sketch, "E167.0", {"points": [v(-139.7, -609.6) * mm, v(-139.7, -598.23) * mm, v(-139.18, -581.68) * mm, v(-138.5, -560.7) * mm, v(-138.23, -545.57) * mm, v(-138.44, -531.03) * mm, v(-139.2, -519.46) * mm, v(-140.27, -510.53) * mm, v(-141.32, -504) * mm, v(-142.43, -498.7) * mm, v(-143.46, -494.53) * mm, v(-144.3, -491.45) * mm, v(-145.24, -488.39) * mm, v(-146.6, -484.32) * mm, v(-148.52, -479.24) * mm, v(-151.13, -473.14) * mm, v(-155, -465) * mm, v(-160.52, -454.72) * mm, v(-168, -442.17) * mm, v(-176.12, -429.27) * mm, v(-187.45, -411.44) * mm, v(-196.14, -397.18) * mm, v(-201.65, -387.09) * mm]});
            skLineSegment(sketch, "E168", {"start": v(-200.43, -389.3) * mm, "end": v(-202.88, -384.85) * mm});
            skLineSegment(sketch, "E169", {"start": v(0, 0) * mm, "end": v(0, -1066.8) * mm, "construction": true});
            skLineSegment(sketch, "E170.MirrorCS", {"start": v(60.96, -200.66) * mm, "end": v(60.96, -187.1) * mm});
            skLineSegment(sketch, "E171.MirrorCS", {"start": v(60.96, -187.1) * mm, "end": v(216.8, -245.54) * mm});
            skLineSegment(sketch, "E172.MirrorCS", {"start": v(202.88, -384.85) * mm, "end": v(216.8, -245.54) * mm});
            skLineSegment(sketch, "E173.MirrorCS", {"start": v(200.43, -389.3) * mm, "end": v(202.88, -384.85) * mm});
            skLineSegment(sketch, "E174.MirrorCS", {"start": v(139.7, -1032.77) * mm, "end": v(139.7, -609.6) * mm});
            skLineSegment(sketch, "E175.MirrorCS", {"start": v(139.7, -1032.77) * mm, "end": v(127, -1032.77) * mm});
            skFitSpline(sketch, "E176.0", {"points": [v(139.7, -609.6) * mm, v(139.7, -598.23) * mm, v(139.18, -581.68) * mm, v(138.5, -560.7) * mm, v(138.23, -545.57) * mm, v(138.44, -531.03) * mm, v(139.2, -519.46) * mm, v(140.27, -510.53) * mm, v(141.32, -504) * mm, v(142.43, -498.7) * mm, v(143.46, -494.53) * mm, v(144.3, -491.45) * mm, v(145.24, -488.39) * mm, v(146.6, -484.32) * mm, v(148.52, -479.24) * mm, v(151.13, -473.14) * mm, v(155, -465) * mm, v(160.52, -454.72) * mm, v(168, -442.17) * mm, v(176.12, -429.27) * mm, v(187.45, -411.44) * mm, v(196.14, -397.18) * mm, v(201.65, -387.09) * mm]});
            skLineSegment(sketch, "E177.0", {"start": v(-278.46, 44.91) * mm, "end": v(-244.55, -88.24) * mm});
            skLineSegment(sketch, "E177.1", {"start": v(-82.74, -89.81) * mm, "end": v(-244.55, -88.24) * mm});
            skLineSegment(sketch, "E178.0", {"start": v(-296.6, 280.24) * mm, "end": v(-440.17, 674.69) * mm});
            skFitSpline(sketch, "E179.0", {"points": [v(-278.38, 51.49) * mm, v(-275.94, 60.16) * mm, v(-272.03, 78.13) * mm, v(-267.89, 115.99) * mm, v(-269.12, 165.74) * mm, v(-279.14, 225.5) * mm, v(-290.27, 262.83) * mm, v(-296.6, 280.24) * mm]});
            skLineSegment(sketch, "E180", {"start": v(-82.74, -89.81) * mm, "end": v(-82.74, -77.11) * mm});
            skLineSegment(sketch, "E181", {"start": v(-429.4, 682.23) * mm, "end": v(-440.17, 674.69) * mm});
            skLineSegment(sketch, "E182", {"start": v(-278.46, 44.91) * mm, "end": v(-278.38, 51.49) * mm});
            skLineSegment(sketch, "E183.MirrorCS", {"start": v(82.74, -89.81) * mm, "end": v(82.74, -77.11) * mm});
            skLineSegment(sketch, "E184.MirrorCS", {"start": v(82.74, -89.81) * mm, "end": v(244.55, -88.24) * mm});
            skLineSegment(sketch, "E185.MirrorCS", {"start": v(278.46, 44.91) * mm, "end": v(244.55, -88.24) * mm});
            skLineSegment(sketch, "E186.MirrorCS", {"start": v(278.46, 44.91) * mm, "end": v(278.38, 51.49) * mm});
            skLineSegment(sketch, "E187.MirrorCS", {"start": v(296.6, 280.24) * mm, "end": v(440.17, 674.69) * mm});
            skLineSegment(sketch, "E188.MirrorCS", {"start": v(429.4, 682.23) * mm, "end": v(440.17, 674.69) * mm});
            skFitSpline(sketch, "E189.0", {"points": [v(278.38, 51.49) * mm, v(275.94, 60.16) * mm, v(272.03, 78.13) * mm, v(267.89, 115.99) * mm, v(269.12, 165.74) * mm, v(279.14, 225.5) * mm, v(290.27, 262.83) * mm, v(296.6, 280.24) * mm]});
            skLineSegment(sketch, "E190.0", {"start": v(-943.02, -386.15) * mm, "end": v(-1256.36, -667.1) * mm});
            skLineSegment(sketch, "E190.1", {"start": v(-957.4, -242.4) * mm, "end": v(-943.02, -386.15) * mm});
            skLineSegment(sketch, "E190.2", {"start": v(-957.4, -242.4) * mm, "end": v(-1101.15, -228.02) * mm});
            skLineSegment(sketch, "E190.3", {"start": v(-1101.15, -228.02) * mm, "end": v(-1382.1, -541.35) * mm});
            skLineSegment(sketch, "E191", {"start": v(-1256.36, -667.1) * mm, "end": v(-1265.35, -658.11) * mm});
            skLineSegment(sketch, "E192", {"start": v(-1373.11, -550.35) * mm, "end": v(-1382.1, -541.35) * mm});
            skLineSegment(sketch, "E193.MirrorCS", {"start": v(943.02, -386.15) * mm, "end": v(1256.36, -667.1) * mm});
            skLineSegment(sketch, "E194.MirrorCS", {"start": v(957.4, -242.4) * mm, "end": v(943.02, -386.15) * mm});
            skLineSegment(sketch, "E195.MirrorCS", {"start": v(957.4, -242.4) * mm, "end": v(1101.15, -228.02) * mm});
            skLineSegment(sketch, "E196.MirrorCS", {"start": v(1101.15, -228.02) * mm, "end": v(1382.1, -541.35) * mm});
            skLineSegment(sketch, "E197.MirrorCS", {"start": v(1373.11, -550.35) * mm, "end": v(1382.1, -541.35) * mm});
            skLineSegment(sketch, "E198.MirrorCS", {"start": v(1256.36, -667.1) * mm, "end": v(1265.35, -658.11) * mm});
            skLineSegment(sketch, "E199.0", {"start": v(-1615.6, -307.86) * mm, "end": v(-1332.16, 12.6) * mm});
            skLineSegment(sketch, "E199.1", {"start": v(-1187.34, -132.23) * mm, "end": v(-1332.16, 12.6) * mm});
            skLineSegment(sketch, "E199.2", {"start": v(-1507.8, -415.66) * mm, "end": v(-1187.34, -132.23) * mm});
            skLineSegment(sketch, "E200", {"start": v(-1507.8, -415.66) * mm, "end": v(-1516.8, -406.66) * mm});
            skLineSegment(sketch, "E201", {"start": v(-1606.6, -316.86) * mm, "end": v(-1615.6, -307.86) * mm});
            skLineSegment(sketch, "E202.MirrorCS", {"start": v(1507.8, -415.66) * mm, "end": v(1516.8, -406.66) * mm});
            skLineSegment(sketch, "E203.MirrorCS", {"start": v(1606.6, -316.86) * mm, "end": v(1615.6, -307.86) * mm});
            skLineSegment(sketch, "E204.MirrorCS", {"start": v(1615.6, -307.86) * mm, "end": v(1332.16, 12.6) * mm});
            skLineSegment(sketch, "E205.MirrorCS", {"start": v(1507.8, -415.66) * mm, "end": v(1187.34, -132.23) * mm});
            skLineSegment(sketch, "E206.MirrorCS", {"start": v(1187.34, -132.23) * mm, "end": v(1332.16, 12.6) * mm});
            skFitSpline(sketch, "E207.0", {"points": [v(-812.8, -609.6) * mm, v(-812.8, -590.02) * mm, v(-810.36, -549.66) * mm, v(-799.38, -488.18) * mm, v(-781.05, -428.52) * mm, v(-763.84, -391.8) * mm, v(-753.95, -374.65) * mm]});
            skLineSegment(sketch, "E207.1", {"start": v(-850.95, -1032.77) * mm, "end": v(-812.8, -609.03) * mm});
            skLineSegment(sketch, "E208", {"start": v(-850.95, -1032.77) * mm, "end": v(-838.2, -1032.77) * mm});
            skLineSegment(sketch, "E209", {"start": v(-757.53, -381) * mm, "end": v(-742.95, -381) * mm});
            skFitSpline(sketch, "E210.0", {"points": [v(-558.8, -609.6) * mm, v(-558.8, -598.47) * mm, v(-559.24, -576.66) * mm, v(-561.4, -545.23) * mm, v(-564.65, -520.1) * mm, v(-568.22, -500.63) * mm, v(-570.87, -488.72) * mm, v(-573.27, -479.35) * mm, v(-575.84, -470.09) * mm, v(-579.4, -458.66) * mm, v(-584.24, -445.08) * mm, v(-591.47, -427) * mm, v(-601.98, -404.14) * mm, v(-612.04, -384.93) * mm, v(-617.5, -374.91) * mm]});
            skLineSegment(sketch, "E210.1", {"start": v(-558.8, -609.03) * mm, "end": v(-520.65, -1032.77) * mm});
            skLineSegment(sketch, "E211", {"start": v(-533.4, -1032.77) * mm, "end": v(-520.65, -1032.77) * mm});
            skLineSegment(sketch, "E212", {"start": v(-628.65, -381) * mm, "end": v(-614.2, -381) * mm});
            skLineSegment(sketch, "E213.MirrorCS", {"start": v(558.8, -609.03) * mm, "end": v(520.65, -1032.77) * mm});
            skLineSegment(sketch, "E214.MirrorCS", {"start": v(628.65, -381) * mm, "end": v(614.2, -381) * mm});
            skLineSegment(sketch, "E215.MirrorCS", {"start": v(533.4, -1032.77) * mm, "end": v(520.65, -1032.77) * mm});
            skLineSegment(sketch, "E216.MirrorCS", {"start": v(850.95, -1032.77) * mm, "end": v(838.2, -1032.77) * mm});
            skLineSegment(sketch, "E217.MirrorCS", {"start": v(850.95, -1032.77) * mm, "end": v(812.8, -609.03) * mm});
            skLineSegment(sketch, "E218.MirrorCS", {"start": v(757.53, -381) * mm, "end": v(742.95, -381) * mm});
            skFitSpline(sketch, "E219.0", {"points": [v(558.8, -609.6) * mm, v(558.8, -598.47) * mm, v(559.24, -576.66) * mm, v(561.4, -545.23) * mm, v(564.65, -520.1) * mm, v(568.22, -500.63) * mm, v(570.87, -488.72) * mm, v(573.27, -479.35) * mm, v(575.84, -470.09) * mm, v(579.4, -458.66) * mm, v(584.24, -445.08) * mm, v(591.47, -427) * mm, v(601.98, -404.14) * mm, v(612.04, -384.93) * mm, v(617.5, -374.91) * mm]});
            skFitSpline(sketch, "E220.0", {"points": [v(812.8, -609.6) * mm, v(812.8, -590.02) * mm, v(810.36, -549.66) * mm, v(799.38, -488.18) * mm, v(781.05, -428.52) * mm, v(763.84, -391.8) * mm, v(753.95, -374.65) * mm]});
            skSolve(sketch);
        }
        {
            var Q0;
            Q0=makeQuery(id+"F35.imprint","IMPRINT",FACE,{"disambiguationData":[TD([[makeQuery(id+"F35.imprint","IMPRINT",EDGE,{"derivedFrom":sQuery(id+"F35.wireOp",EDGE,"E157.0")}),1.0]])]});
            var Q1;
            Q1=makeQuery(id+"F35.imprint","IMPRINT",FACE,{"disambiguationData":[TD([[makeQuery(id+"F35.imprint","IMPRINT",EDGE,{"derivedFrom":sQuery(id+"F35.wireOp",EDGE,"E157.4")}),1.0]])]});
            var Q2;
            Q2=makeQuery(id+"F35.imprint","IMPRINT",FACE,{"disambiguationData":[TD([[makeQuery(id+"F35.imprint","IMPRINT",EDGE,{"derivedFrom":sQuery(id+"F35.wireOp",EDGE,"E158.0")}),1.0]])]});
            var Q3;
            Q3=makeQuery(id+"F35.imprint","IMPRINT",FACE,{"disambiguationData":[TD([[makeQuery(id+"F35.imprint","IMPRINT",EDGE,{"derivedFrom":sQuery(id+"F35.wireOp",EDGE,"E158.1")}),1.0]])]});
            var Q4;
            Q4=makeQuery(id+"F35.imprint","IMPRINT",FACE,{"disambiguationData":[TD([[makeQuery(id+"F35.imprint","IMPRINT",EDGE,{"derivedFrom":sQuery(id+"F35.wireOp",EDGE,"E160.0")}),1.0]])]});
            var Q5;
            Q5=makeQuery(id+"F35.imprint","IMPRINT",FACE,{"disambiguationData":[TD([[makeQuery(id+"F35.imprint","IMPRINT",EDGE,{"derivedFrom":sQuery(id+"F35.wireOp",EDGE,"E160.2")}),-1.0]])]});
            var Q6;
            Q6=makeQuery(id+"F35.imprint","IMPRINT",FACE,{"disambiguationData":[TD([[makeQuery(id+"F35.imprint","IMPRINT",EDGE,{"derivedFrom":sQuery(id+"F35.wireOp",EDGE,"E161.0")}),-1.0]])]});
            var Q7;
            Q7=makeQuery(id+"F35.imprint","IMPRINT",FACE,{"disambiguationData":[TD([[makeQuery(id+"F35.imprint","IMPRINT",EDGE,{"derivedFrom":sQuery(id+"F35.wireOp",EDGE,"E161.4")}),1.0]])]});
            var Q8;
            Q8=makeQuery(id+"F35.imprint","IMPRINT",FACE,{"disambiguationData":[TD([[makeQuery(id+"F35.imprint","IMPRINT",EDGE,{"derivedFrom":sQuery(id+"F35.wireOp",EDGE,"E162.4")}),-1.0]])]});
            var Q9;
            Q9=makeQuery(id+"F35.imprint","IMPRINT",FACE,{"disambiguationData":[TD([[makeQuery(id+"F35.imprint","IMPRINT",EDGE,{"derivedFrom":sQuery(id+"F35.wireOp",EDGE,"E162.0")}),1.0]])]});
            var Q10;
            Q10=makeQuery(id+"F35.imprint","IMPRINT",FACE,{"disambiguationData":[TD([[makeQuery(id+"F35.imprint","IMPRINT",EDGE,{"derivedFrom":sQuery(id+"F35.wireOp",EDGE,"E159.0")}),1.0]])]});
            var Q11;
            Q11=makeQuery(id+"F35.imprint","IMPRINT",FACE,{"disambiguationData":[TD([[makeQuery(id+"F35.imprint","IMPRINT",EDGE,{"derivedFrom":sQuery(id+"F35.wireOp",EDGE,"E159.4")}),-1.0]])]});
            var Q12;
            Q12=makeQuery(id+"F34.opExtrude","CAP_FACE",FACE,{"disambiguationData":[OSD([sQuery(id+"F33.wireOp",EDGE,"E41"),sQuery(id+"F33.wireOp",EDGE,"E43"),sQuery(id+"F33.wireOp",EDGE,"E47"),sQuery(id+"F33.wireOp",EDGE,"E52"),sQuery(id+"F33.wireOp",EDGE,"E53"),sQuery(id+"F33.wireOp",EDGE,"E54.MirrorCS"),sQuery(id+"F33.wireOp",EDGE,"E55.MirrorCS"),sQuery(id+"F33.wireOp",EDGE,"E56.MirrorCS"),sQuery(id+"F33.wireOp",EDGE,"E57.MirrorCS"),sQuery(id+"F33.wireOp",EDGE,"E58.MirrorCS"),sQuery(id+"F33.wireOp",EDGE,"E60")])],"isStart":true});
            extrude(context, id + "F36", {"entities" : qUnion([Q0, Q1, Q2, Q3, Q4, Q5, Q6, Q7, Q8, Q9, Q10, Q11]), "operationType" : NewBodyOperationType.ADD, "endBound" : BoundingType.UP_TO_SURFACE, "oppositeDirection" : true, "depth" : 25.4 * mm, "endBoundEntityFace" : qUnion([Q12]), "offsetDistance" : 25.4 * mm});
        }
        {
            var Q0;
            Q0=makeQuery(id+"F33.imprint","IMPRINT",FACE,{"disambiguationData":[TD([[makeQuery(id+"F33.imprint","IMPRINT",EDGE,{"derivedFrom":sQuery(id+"F33.wireOp",EDGE,"E150.bottom")}),-1.0]])]});
            extrude(context, id + "F37", {"entities" : qUnion([Q0]), "depth" : 3.17 * mm, "offsetDistance" : 25.4 * mm});
        }
    });
